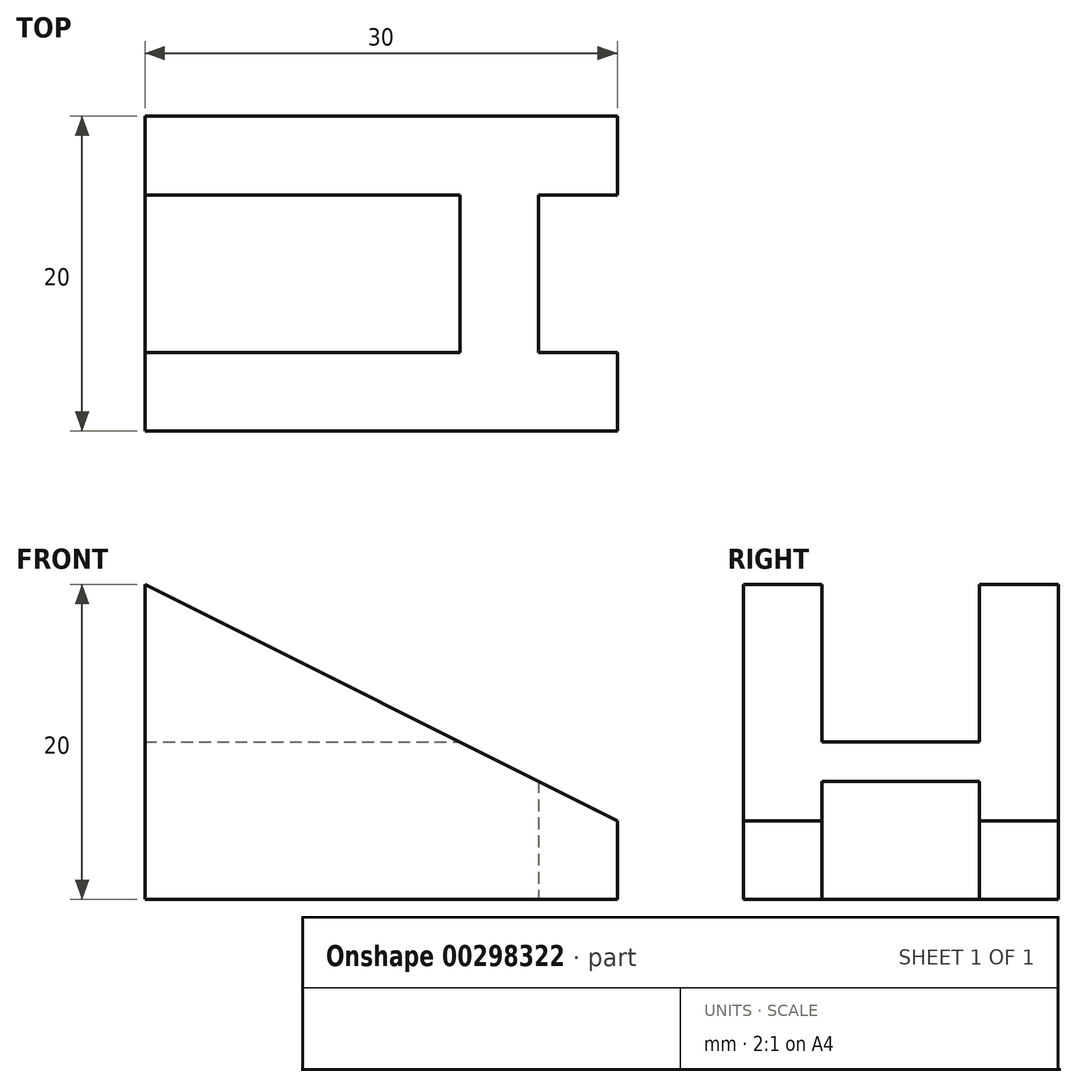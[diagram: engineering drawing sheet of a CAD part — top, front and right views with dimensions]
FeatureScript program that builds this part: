
annotation { "Feature Type Name" : "Feature", "Feature Type Description" : "" }
export const myFeature = defineFeature(function(context is Context, id is Id, definition is map)
    precondition{}
    {
        {
            var Q0;
            Q0=qCreatedBy(makeId("Front.planeOp"),FACE);
            var sketch = newSketch(context, id + "F0", { "sketchPlane" : qUnion([Q0])});
            skLineSegment(sketch, "E0.bottom", {"start": v(0, 0) * mm, "end": v(30, 0) * mm});
            skLineSegment(sketch, "E0.left", {"start": v(0, 0) * mm, "end": v(0, 20) * mm});
            skLineSegment(sketch, "E1", {"start": v(30, 0) * mm, "end": v(30, 5) * mm});
            skLineSegment(sketch, "E2", {"start": v(30, 5) * mm, "end": v(0, 20) * mm});
            skSolve(sketch);
        }
        {
            var Q0;
            Q0 = qSketchRegion(id + "F0", true);
            extrude(context, id + "F1", {"entities" : qUnion([Q0]), "depth" : 5 * mm});
        }
        {
            var Q0;
            Q0=qCreatedBy(makeId("Top.planeOp"),FACE);
            var sketch = newSketch(context, id + "F2", { "sketchPlane" : qUnion([Q0])});
            skLineSegment(sketch, "E3.bottom", {"start": v(0, 0) * mm, "end": v(20, 0) * mm});
            skLineSegment(sketch, "E3.top", {"start": v(0, 10) * mm, "end": v(20, 10) * mm});
            skLineSegment(sketch, "E3.left", {"start": v(0, 0) * mm, "end": v(0, 10) * mm});
            skLineSegment(sketch, "E3.right", {"start": v(20, 0) * mm, "end": v(20, 10) * mm});
            skSolve(sketch);
        }
        {
            var Q0;
            Q0 = qSketchRegion(id + "F2", true);
            extrude(context, id + "F3", {"entities" : qUnion([Q0]), "operationType" : NewBodyOperationType.ADD, "depth" : 10 * mm});
        }
        {
            var Q0;
            Q0=makeQuery(id+"F3.opExtrude","SWEPT_FACE",FACE,{"disambiguationData":[OSD([sQuery(id+"F2.wireOp",EDGE,"E3.top")])]});
            var sketch = newSketch(context, id + "F4", { "sketchPlane" : qUnion([Q0])});
            skPoint(sketch, "E4.endSnap0", {"position": v(0, 5) * mm});
            skLineSegment(sketch, "E5", {"start": v(0, 0) * mm, "end": v(0, 20) * mm});
            skLineSegment(sketch, "E6", {"start": v(0, 0) * mm, "end": v(-30, 0) * mm});
            skLineSegment(sketch, "E7", {"start": v(-30, 0) * mm, "end": v(-30, 5) * mm});
            skLineSegment(sketch, "E8", {"start": v(-30, 5) * mm, "end": v(0, 20) * mm});
            skSolve(sketch);
        }
        {
            var Q0;
            Q0 = qSketchRegion(id + "F4", true);
            extrude(context, id + "F5", {"entities" : qUnion([Q0]), "operationType" : NewBodyOperationType.ADD, "depth" : 5 * mm});
        }
        {
            var Q0;
            {var subQ0=sQuery(id+"F0.wireOp",EDGE,"E1");var subQ1=sQuery(id+"F0.wireOp",EDGE,"E2");var subQ2=sQuery(id+"F0.wireOp",EDGE,"E0.bottom");var subQ3=makeQuery(id+"F1.opExtrude","CAP_FACE",FACE,{"disambiguationData":[OSD([subQ2,sQuery(id+"F0.wireOp",EDGE,"E0.left"),subQ0,subQ1])],"isStart":true});Q0=makeQuery(id+"F3.boolean.opBoolean","SPLIT",FACE,{"disambiguationData":[TD([makeQuery(id+"F1.opExtrude","SWEPT_FACE",FACE,{"disambiguationData":[OSD([subQ2])]})])],"derivedFrom":subQ3});}
            var sketch = newSketch(context, id + "F6", { "sketchPlane" : qUnion([Q0])});
            skLineSegment(sketch, "E9", {"start": v(-25, 7.5) * mm, "end": v(-25, 0) * mm});
            skSolve(sketch);
        }
        {
            var Q0;
            {var subQ0=sQuery(id+"F6.wireOp",EDGE,"E9");Q0=makeQuery(id+"F6.imprint","IMPRINT",FACE,{"disambiguationData":[TD([[makeQuery(id+"F6.imprint","IMPRINT",EDGE,{"derivedFrom":subQ0}),1.0]])]});}
            extrude(context, id + "F7", {"entities" : qUnion([Q0]), "operationType" : NewBodyOperationType.ADD, "endBound" : BoundingType.UP_TO_NEXT, "depth" : 25 * mm});
        }
    });
